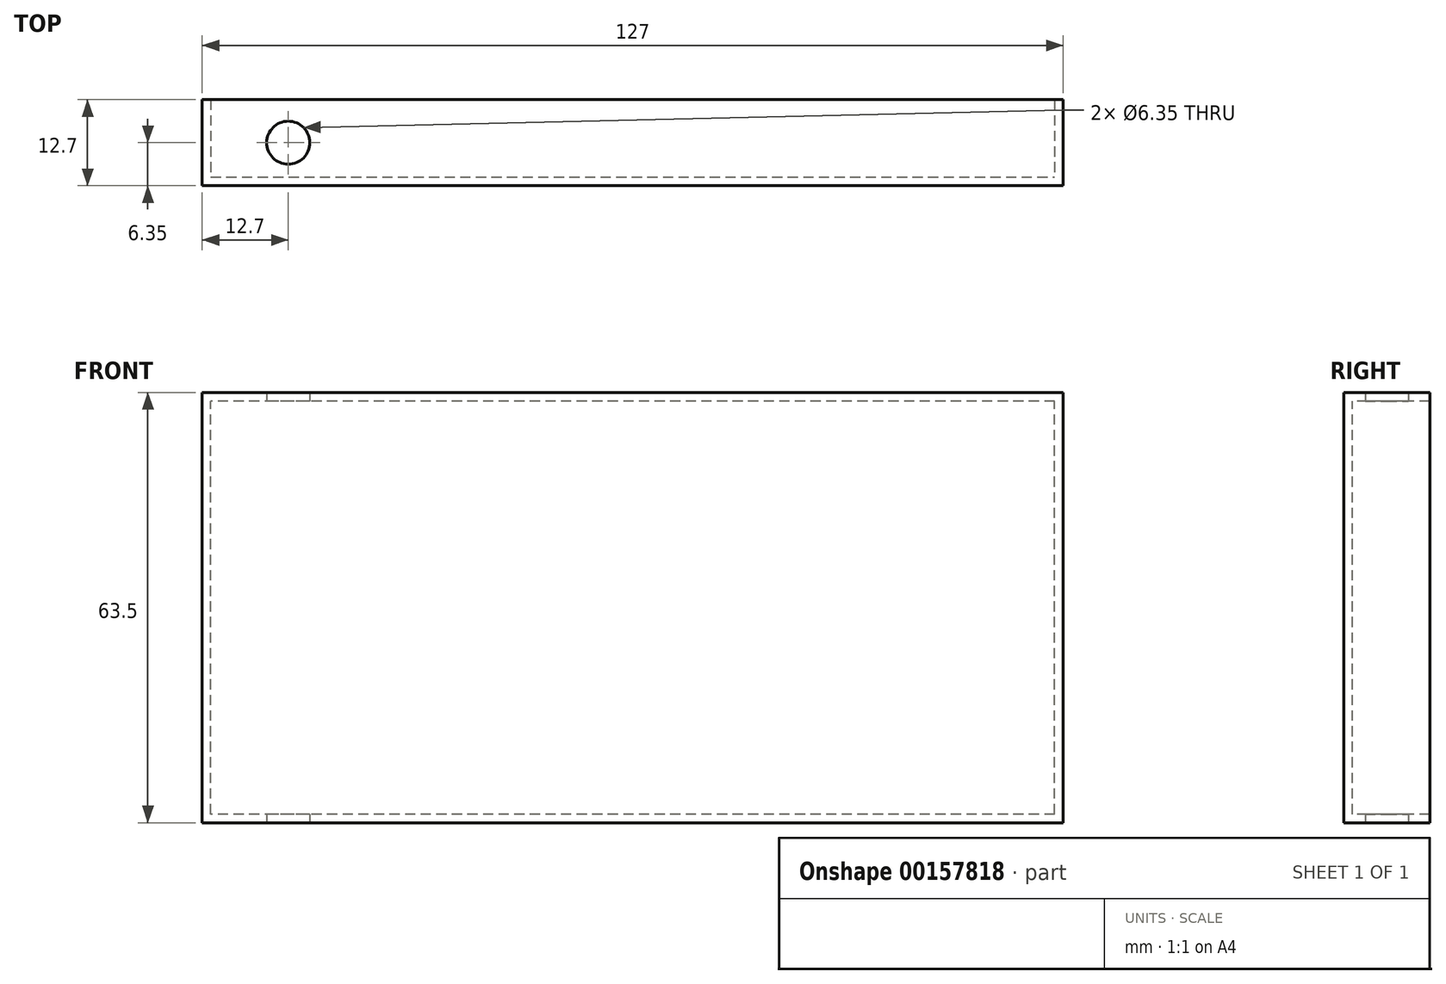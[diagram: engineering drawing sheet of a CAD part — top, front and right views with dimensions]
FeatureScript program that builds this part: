
annotation { "Feature Type Name" : "Feature", "Feature Type Description" : "" }
export const myFeature = defineFeature(function(context is Context, id is Id, definition is map)
    precondition{}
    {
        {
            var Q0;
            Q0=qCreatedBy(makeId("Top.planeOp"),FACE);
            var sketch = newSketch(context, id + "F0", { "sketchPlane" : qUnion([Q0])});
            skLineSegment(sketch, "E0.bottom", {"start": v(63.5, -6.35) * mm, "end": v(-63.5, -6.35) * mm});
            skLineSegment(sketch, "E0.top", {"start": v(63.5, 6.35) * mm, "end": v(-63.5, 6.35) * mm});
            skLineSegment(sketch, "E0.left", {"start": v(63.5, -6.35) * mm, "end": v(63.5, 6.35) * mm});
            skLineSegment(sketch, "E0.right", {"start": v(-63.5, -6.35) * mm, "end": v(-63.5, 6.35) * mm});
            skPoint(sketch, "E0.middle", {"position": v(0, 0) * mm});
            skCircle(sketch, "E1", {"center": v(-50.8, 0) * mm, "radius": 3.18 * mm});
            skLineSegment(sketch, "E2", {"start": v(-62.23, 6.35) * mm, "end": v(-62.23, -6.35) * mm});
            skLineSegment(sketch, "E3", {"start": v(62.23, 6.35) * mm, "end": v(62.23, -6.35) * mm});
            skLineSegment(sketch, "E4", {"start": v(-62.23, -5.08) * mm, "end": v(63.5, -5.08) * mm});
            skSolve(sketch);
        }
        {
            var Q0;
            Q0 = qSketchRegion(id + "F0", true);
            extrude(context, id + "F1", {"entities" : qUnion([Q0]), "endBound" : BoundingType.SYMMETRIC, "depth" : 63.5 * mm});
        }
        {
            var Q0;
            Q0=makeQuery(id+"F0.imprint","IMPRINT",FACE,{"disambiguationData":[TD([[makeQuery(id+"F0.imprint","IMPRINT",EDGE,{"derivedFrom":sQuery(id+"F0.wireOp",EDGE,"E1")}),-1.0]])]});
            extrude(context, id + "F2", {"entities" : qUnion([Q0]), "operationType" : NewBodyOperationType.REMOVE, "endBound" : BoundingType.SYMMETRIC, "oppositeDirection" : true, "depth" : 60.96 * mm});
        }
    });
